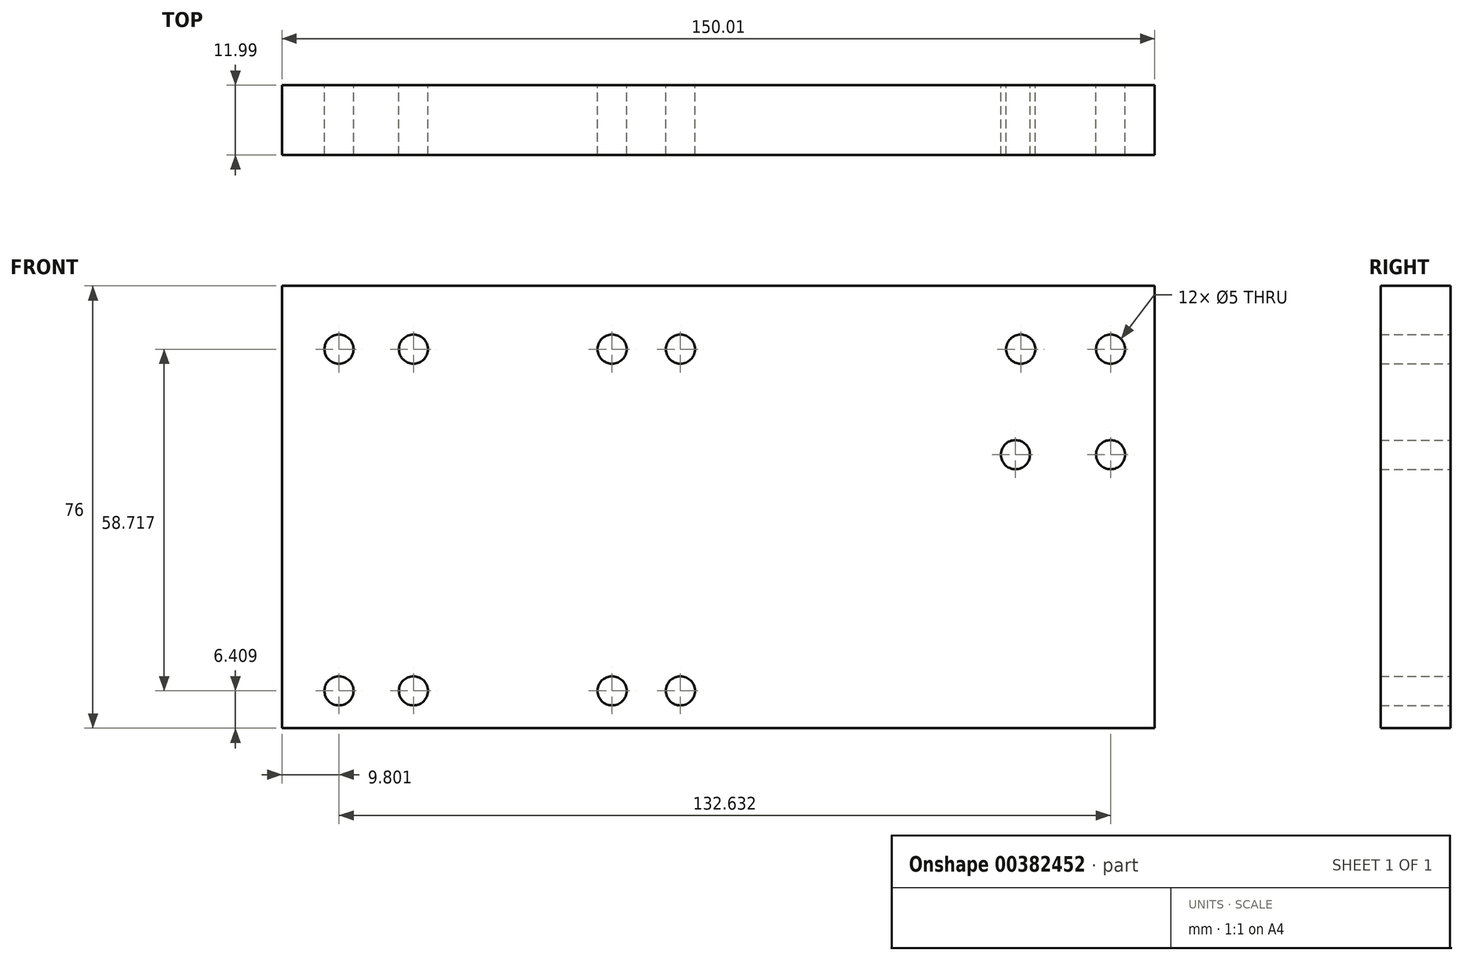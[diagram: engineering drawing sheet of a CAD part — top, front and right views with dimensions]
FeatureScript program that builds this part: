
annotation { "Feature Type Name" : "Feature", "Feature Type Description" : "" }
export const myFeature = defineFeature(function(context is Context, id is Id, definition is map)
    precondition{}
    {
        {
            var Q0;
            Q0=qCreatedBy(makeId("Front.planeOp"),FACE);
            var sketch = newSketch(context, id + "F0", { "sketchPlane" : qUnion([Q0])});
            skLineSegment(sketch, "E0", {"start": v(-56.74, 29) * mm, "end": v(-56.74, -46.99) * mm});
            skLineSegment(sketch, "E1", {"start": v(-56.74, 29) * mm, "end": v(93.27, 29) * mm});
            skLineSegment(sketch, "E2", {"start": v(-56.74, -46.99) * mm, "end": v(93.27, -46.99) * mm});
            skLineSegment(sketch, "E3", {"start": v(93.27, -46.99) * mm, "end": v(93.27, 29) * mm});
            skCircle(sketch, "E4", {"center": v(-46.94, 18.14) * mm, "radius": 2.5 * mm});
            skCircle(sketch, "E5", {"center": v(-34.14, 18.14) * mm, "radius": 2.5 * mm});
            skCircle(sketch, "E6", {"center": v(-34.14, -40.58) * mm, "radius": 2.5 * mm});
            skCircle(sketch, "E7", {"center": v(-46.94, -40.58) * mm, "radius": 2.5 * mm});
            skCircle(sketch, "E8", {"center": v(0, 18.14) * mm, "radius": 2.5 * mm});
            skCircle(sketch, "E9", {"center": v(11.75, 18.14) * mm, "radius": 2.5 * mm});
            skCircle(sketch, "E10", {"center": v(0, -40.58) * mm, "radius": 2.5 * mm});
            skCircle(sketch, "E11", {"center": v(11.75, -40.58) * mm, "radius": 2.5 * mm});
            skCircle(sketch, "E12", {"center": v(70.24, 18.14) * mm, "radius": 2.5 * mm});
            skCircle(sketch, "E13", {"center": v(85.7, 18.14) * mm, "radius": 2.5 * mm});
            skCircle(sketch, "E14", {"center": v(85.7, 0) * mm, "radius": 2.5 * mm});
            skCircle(sketch, "E15", {"center": v(69.33, 0) * mm, "radius": 2.5 * mm});
            skSolve(sketch);
        }
        {
            var Q0;
            Q0 = qSketchRegion(id + "F0", true);
            extrude(context, id + "F1", {"entities" : qUnion([Q0]), "depth" : 12 * mm});
        }
    });
